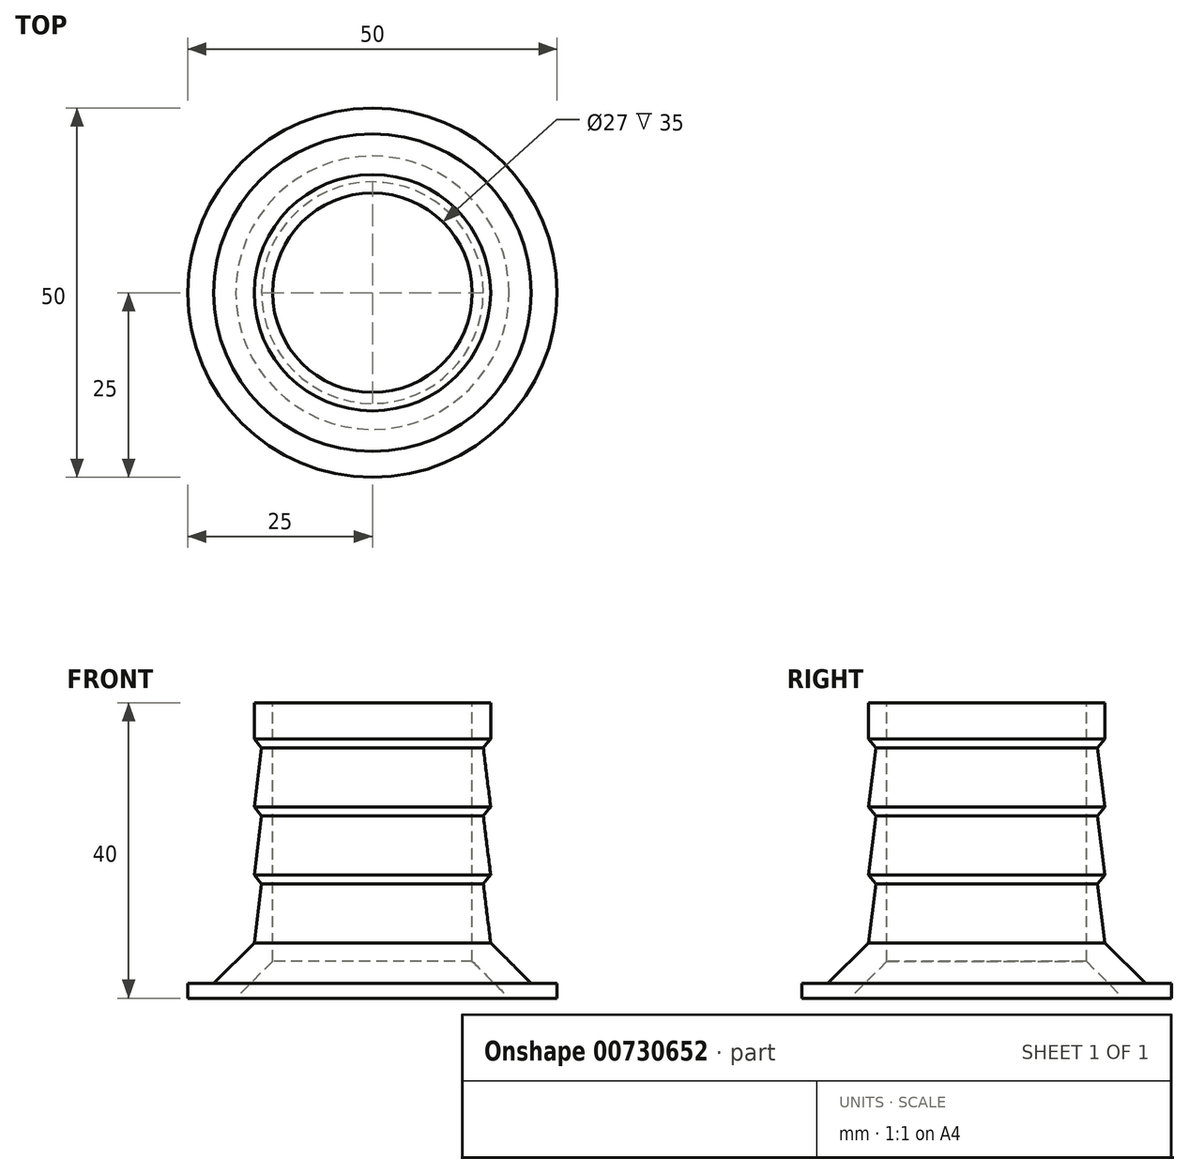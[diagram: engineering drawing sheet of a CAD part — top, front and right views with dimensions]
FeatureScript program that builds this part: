
annotation { "Feature Type Name" : "Feature", "Feature Type Description" : "" }
export const myFeature = defineFeature(function(context is Context, id is Id, definition is map)
    precondition{}
    {
        {
            var Q0;
            Q0=qCreatedBy(makeId("Front.planeOp"),FACE);
            var sketch = newSketch(context, id + "F0", { "sketchPlane" : qUnion([Q0])});
            skLineSegment(sketch, "E0", {"start": v(0, 31.96) * mm, "end": v(0, -32.93) * mm, "construction": true});
            skLineSegment(sketch, "E1", {"start": v(-13.5, 0) * mm, "end": v(-25, 0) * mm});
            skLineSegment(sketch, "E2", {"start": v(-25, 0) * mm, "end": v(-25, 2) * mm});
            skLineSegment(sketch, "E3", {"start": v(-25, 2) * mm, "end": v(-21.5, 2) * mm});
            skLineSegment(sketch, "E4", {"start": v(-21.5, 2) * mm, "end": v(-16, 7.5) * mm});
            skLineSegment(sketch, "E5", {"start": v(-16, 7.5) * mm, "end": v(-16, 40) * mm, "construction": true});
            skLineSegment(sketch, "E6", {"start": v(-16, 40) * mm, "end": v(-13.5, 40) * mm});
            skLineSegment(sketch, "E7", {"start": v(-13.5, 40) * mm, "end": v(-13.5, 0) * mm});
            skLineSegment(sketch, "E8", {"start": v(-16, 7.5) * mm, "end": v(-15, 15.5) * mm});
            skLineSegment(sketch, "E9", {"start": v(-15, 15.5) * mm, "end": v(-16, 16.7) * mm});
            skLineSegment(sketch, "E10", {"start": v(-16, 16.7) * mm, "end": v(-15, 24.7) * mm});
            skLineSegment(sketch, "E11", {"start": v(-15, 24.7) * mm, "end": v(-16, 25.9) * mm});
            skLineSegment(sketch, "E12", {"start": v(-16, 25.9) * mm, "end": v(-15, 33.9) * mm});
            skLineSegment(sketch, "E13", {"start": v(-15, 33.9) * mm, "end": v(-16, 35.1) * mm});
            skLineSegment(sketch, "E14", {"start": v(-16, 35.1) * mm, "end": v(-16, 40) * mm});
            skLineSegment(sketch, "E15", {"start": v(-15, 4.85) * mm, "end": v(-15, 51.56) * mm, "construction": true});
            skSolve(sketch);
        }
        {
            var Q0;
            Q0 = qSketchRegion(id + "F0", true);
            var Q1;
            Q1=sQuery(id+"F0.wireOp",EDGE,"E0");
            revolve(context, id + "F1", {"surfaceOperationType" : NewSurfaceOperationType.NEW, "entities" : qUnion([Q0]), "axis" : qUnion([Q1]), "revolveType" : RevolveType.FULL});
        }
        {
            var Q0;
            Q0=makeQuery(id+"F1.opRevolve","SWEPT_EDGE",EDGE,{"disambiguationData":[OSD([sQuery(id+"F0.wireOp",EDGE,"E1"),sQuery(id+"F0.wireOp",EDGE,"E7")])]});
            chamfer(context, id + "F2", {"entities" : qUnion([Q0]), "width" : 5 * mm, "tangentPropagation" : true});
        }
    });
